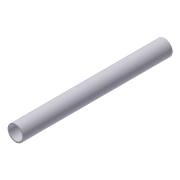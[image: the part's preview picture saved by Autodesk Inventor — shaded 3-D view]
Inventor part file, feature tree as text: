
AUTODESK INVENTOR PART (.ipt)
format: ipt  version: 2012 (Build 160160000, 160)  size: 80,384 bytes
history: native  units: in
note: dims shown in document units (in); Inventor stores cm internally (conversion verified against a paired STEP export)
features: extrude x2, sketch x2, other x1, projected_geometry x1
ambient origin geometry x8: Origin, YZ Plane, XZ Plane, XY Plane, X Axis, Y Axis, Z Axis, Center Point
bodies: Solid1 (feature_tree)
feature tree (6):
  extrude  "Extrusion1"  Depth=1.375in
  other  "Work Axis1"
  extrude  "Extrusion2"  Depth=0.25in
  sketch  "Sketch1"  dims[d0=1.656in d1=1.375in]
  sketch  "Sketch2"  dims[d2=15.5in d3=0.0in d4=0.25in d5=2.0in d6=1.25in d7=1.0in d8=0.0in]
  projected_geometry  "Projected Loop1"
